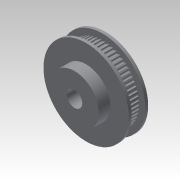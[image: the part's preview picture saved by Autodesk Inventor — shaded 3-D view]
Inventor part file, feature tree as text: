
AUTODESK INVENTOR PART (.ipt)
format: ipt  version: 2020 (Build 240168000, 168)  size: 245,248 bytes
history: native  units: mm
features: sketch x2, revolve x1, extrude x1, pattern_circular x1
ambient origin geometry x8: Origin, YZ Plane, XZ Plane, XY Plane, X Axis, Y Axis, Z Axis, Center Point
bodies: Solid1 (feature_tree)
feature tree (5):
  revolve  "Revolution1"  [1 undecoded]
  extrude  "Extrusion1"  Depth=18.95mm
  pattern_circular  "Circular Pattern1"  Angle=90.0deg  [1 undecoded]
  sketch  "Sketch1"  dims[d0=4.0mm d1=7.0mm]
  sketch  "Sketch2"  dims[d4=1.5mm d6=18.95mm d7=90.0deg d8=1.3mm d9=18.85mm d10=10.0mm d11=0.0mm d12=600.0mm d13=360.0deg d15=22.0mm d16=6.0mm d17=12.5mm]
note: 2 required parameter values undecoded (feature->parameter linkage not recoverable at this tier; creation-order binding heuristic only, values carry confidence <= 0.55)